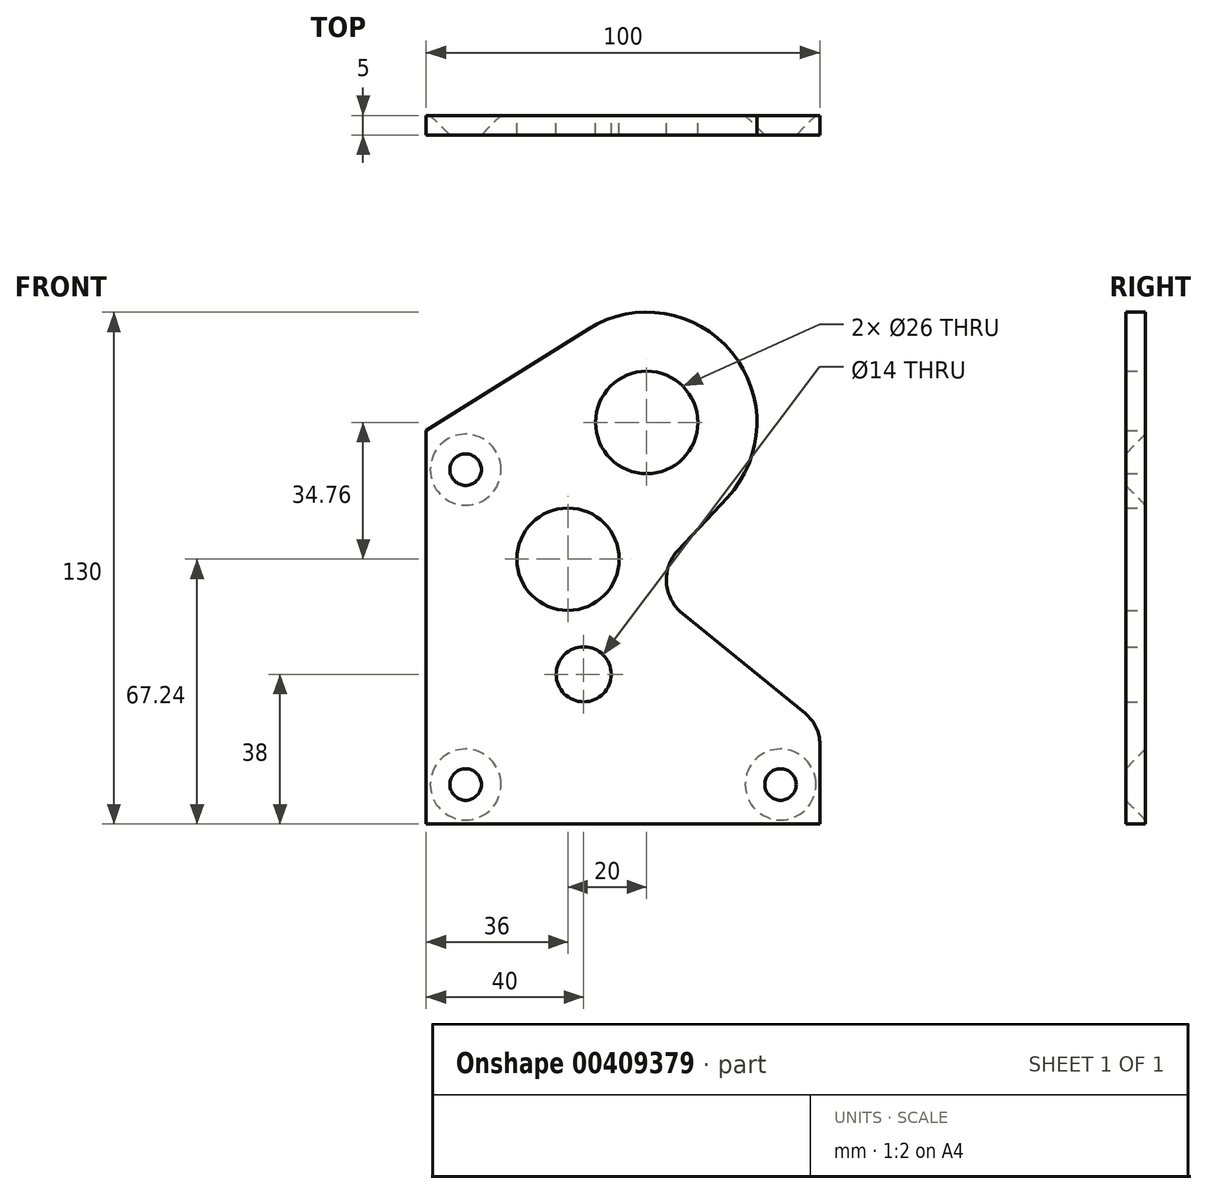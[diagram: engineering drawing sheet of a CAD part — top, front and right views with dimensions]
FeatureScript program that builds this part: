
annotation { "Feature Type Name" : "Feature", "Feature Type Description" : "" }
export const myFeature = defineFeature(function(context is Context, id is Id, definition is map)
    precondition{}
    {
        {
            var Q0;
            Q0=qCreatedBy(makeId("Front.planeOp"),FACE);
            var sketch = newSketch(context, id + "F0", { "sketchPlane" : qUnion([Q0])});
            skLineSegment(sketch, "E0", {"start": v(0, 0) * mm, "end": v(0, 100) * mm});
            skLineSegment(sketch, "E1", {"start": v(0, 0) * mm, "end": v(100, 0) * mm});
            skLineSegment(sketch, "E2", {"start": v(100, 0) * mm, "end": v(100, 25) * mm});
            skCircle(sketch, "E3", {"center": v(56, 102) * mm, "radius": 13 * mm});
            skArc(sketch, "E4", {"start": v(76.46, 82.88) * mm, "mid": v(77.61, 119.8) * mm, "end": v(41.15, 125.74) * mm});
            skLineSegment(sketch, "E5", {"start": v(0, 100) * mm, "end": v(41.15, 125.74) * mm});
            skArc(sketch, "E6", {"start": v(63.96, 69.51) * mm, "mid": v(61.03, 61.25) * mm, "end": v(65.05, 53.47) * mm});
            skLineSegment(sketch, "E7", {"start": v(100, 25) * mm, "end": v(65.05, 53.47) * mm});
            skLineSegment(sketch, "E8", {"start": v(63.96, 69.51) * mm, "end": v(76.46, 82.88) * mm});
            skCircle(sketch, "E9", {"center": v(90, 10) * mm, "radius": 4 * mm});
            skCircle(sketch, "E10", {"center": v(10, 10) * mm, "radius": 4 * mm});
            skCircle(sketch, "E11", {"center": v(10, 90) * mm, "radius": 4 * mm});
            skCircle(sketch, "E12", {"center": v(36, 67.24) * mm, "radius": 13 * mm});
            skCircle(sketch, "E13", {"center": v(40, 38) * mm, "radius": 7 * mm});
            skSolve(sketch);
        }
        {
            var Q0;
            Q0=makeQuery(id+"F0.imprint","IMPRINT",FACE,{"disambiguationData":[TD([[makeQuery(id+"F0.imprint","IMPRINT",EDGE,{"derivedFrom":sQuery(id+"F0.wireOp",EDGE,"E0")}),-1.0]])]});
            extrude(context, id + "F1", {"entities" : qUnion([Q0]), "depth" : 5 * mm});
        }
        {
            var Q0;
            Q0=makeQuery(id+"F1.opExtrude","CAP_EDGE",EDGE,{"disambiguationData":[OSD([sQuery(id+"F0.wireOp",EDGE,"E9")])],"isStart":true});
            var Q1;
            Q1=makeQuery(id+"F1.opExtrude","CAP_EDGE",EDGE,{"disambiguationData":[OSD([sQuery(id+"F0.wireOp",EDGE,"E10")])],"isStart":true});
            var Q2;
            Q2=makeQuery(id+"F1.opExtrude","CAP_EDGE",EDGE,{"disambiguationData":[OSD([sQuery(id+"F0.wireOp",EDGE,"E11")])],"isStart":true});
            chamfer(context, id + "F2", {"entities" : qUnion([Q0, Q1, Q2]), "width" : 5 * mm, "tangentPropagation" : true});
        }
        {
            var Q0;
            Q0=makeQuery(id+"F1.opExtrude","SWEPT_EDGE",EDGE,{"disambiguationData":[OSD([sQuery(id+"F0.wireOp",EDGE,"E2"),sQuery(id+"F0.wireOp",EDGE,"E7")])]});
            fillet(context, id + "F3", {"entities" : qUnion([Q0]), "radius" : 10 * mm, "tangentPropagation" : true, "allowEdgeOverflow" : false});
        }
    });
